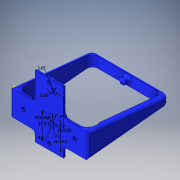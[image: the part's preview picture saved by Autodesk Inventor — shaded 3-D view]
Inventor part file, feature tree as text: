
AUTODESK INVENTOR PART (.ipt)
format: ipt  version: 2016 (Build 200138000, 138)  size: 570,880 bytes
history: native  units: in
note: dims shown in document units (in); Inventor stores cm internally (conversion verified against a paired STEP export)
features: fillet x12, sketch x10, extrude x8, hole x2
ambient origin geometry x8: Origin, YZ Plane, XZ Plane, XY Plane, X Axis, Y Axis, Z Axis, Center Point
bodies: Solid1 (feature_tree)
feature tree (32):
  extrude  "Extrusion1"  Depth=0.5197in
  extrude  "Extrusion10"  Depth=0.0787in
  extrude  "Extrusion11"  Depth=0.2096in TaperAngle=0.0deg
  hole  "Hole2"  [1 undecoded]
  sketch  "Sketch19"  dims[d85=0.562in d86=0.0in d87=0.2953in]
  extrude  "Extrusion12"  Depth=0.2953in
  hole  "Hole3"  [1 undecoded]
  fillet  "Fillet19"  Radius=0.2598in
  fillet  "Fillet20"  Radius=0.2756in
  extrude  "Extrusion13"  Depth=0.0787in
  extrude  "Extrusion15"  Depth=0.1181in
  extrude  "Extrusion16"  Depth=0.2598in
  fillet  "Fillet29"  Radius=0.2756in
  fillet  "Fillet30"  Radius=0.1181in
  extrude  "Extrusion17"  Depth=0.0669in
  fillet  "Fillet34"  Radius=0.0394in
  fillet  "Fillet35"  Radius=0.0787in
  fillet  "Fillet36"  Radius=0.0787in
  fillet  "Fillet37"  Radius=1.6142in
  fillet  "Fillet38"  Radius=0.5197in
  fillet  "Fillet39"  Radius=0.5197in
  fillet  "Fillet40"  Radius=0.1969in
  fillet  "Fillet41"  Radius=0.1614in
  sketch  "Sketch1"  dims[d0=1.6142in d1=0.5197in]
  sketch  "Sketch15"  dims[d2=0.0787in d3=0.0in d79=0.5118in]
  sketch  "Sketch16"  dims[d80=0.5118in d81=0.2096in d82=0.0in]
  sketch  "Sketch17"  dims[d83=0.5118in d84=0.5118in]
  sketch  "Sketch20"  dims[d88=0.2953in d89=0.2598in d90=0.2598in d91=0.2756in]
  sketch  "Sketch22"  dims[d92=0.0787in d93=0.2953in]
  sketch  "Sketch24"  dims[d94=0.2953in d95=0.1181in]
  sketch  "Sketch25"  dims[d96=0.2598in d97=0.2598in d98=0.2756in]
  sketch  "Sketch30"  dims[d99=0.0787in d100=0.2362in d101=0.1575in d102=0.0787in d103=90.0deg d104=0.1181in d105=0.8108in d108=0.2835in d110=0.2605in d111=0.2605in d112=0.3622in d113=0.1437in d114=0.5551in d115=0.2224in d116=0.0787in d120=0.1181in d121=0.0in d124=0.0591in d125=0.2362in d126=0.1575in d127=0.0787in d128=90.0deg d129=0.315in d130=0.8108in d131=0.1142in d132=0.0394in d133=0.0787in d134=0.0787in d135=1.6142in d136=0.0in d144=0.5197in d145=0.5197in d147=0.1969in d148=0.1614in d149=0.1614in d150=11.811in d151=0.0in d153=0.0787in d154=0.0787in d155=1.4567in d156=0.0in d162=0.1575in d163=0.0394in d166=0.5591in d168=0.5591in d170=0.8071in d171=0.0984in d172=0.0984in d173=0.8071in d174=0.1181in d175=0.1181in d176=0.0in d177=0.0394in d178=0.0394in d179=0.1181in d180=0.0748in d181=0.1181in d182=0.0591in d183=0.0787in d184=0.0669in]
note: 2 required parameter values undecoded (feature->parameter linkage not recoverable at this tier; creation-order binding heuristic only, values carry confidence <= 0.55)
